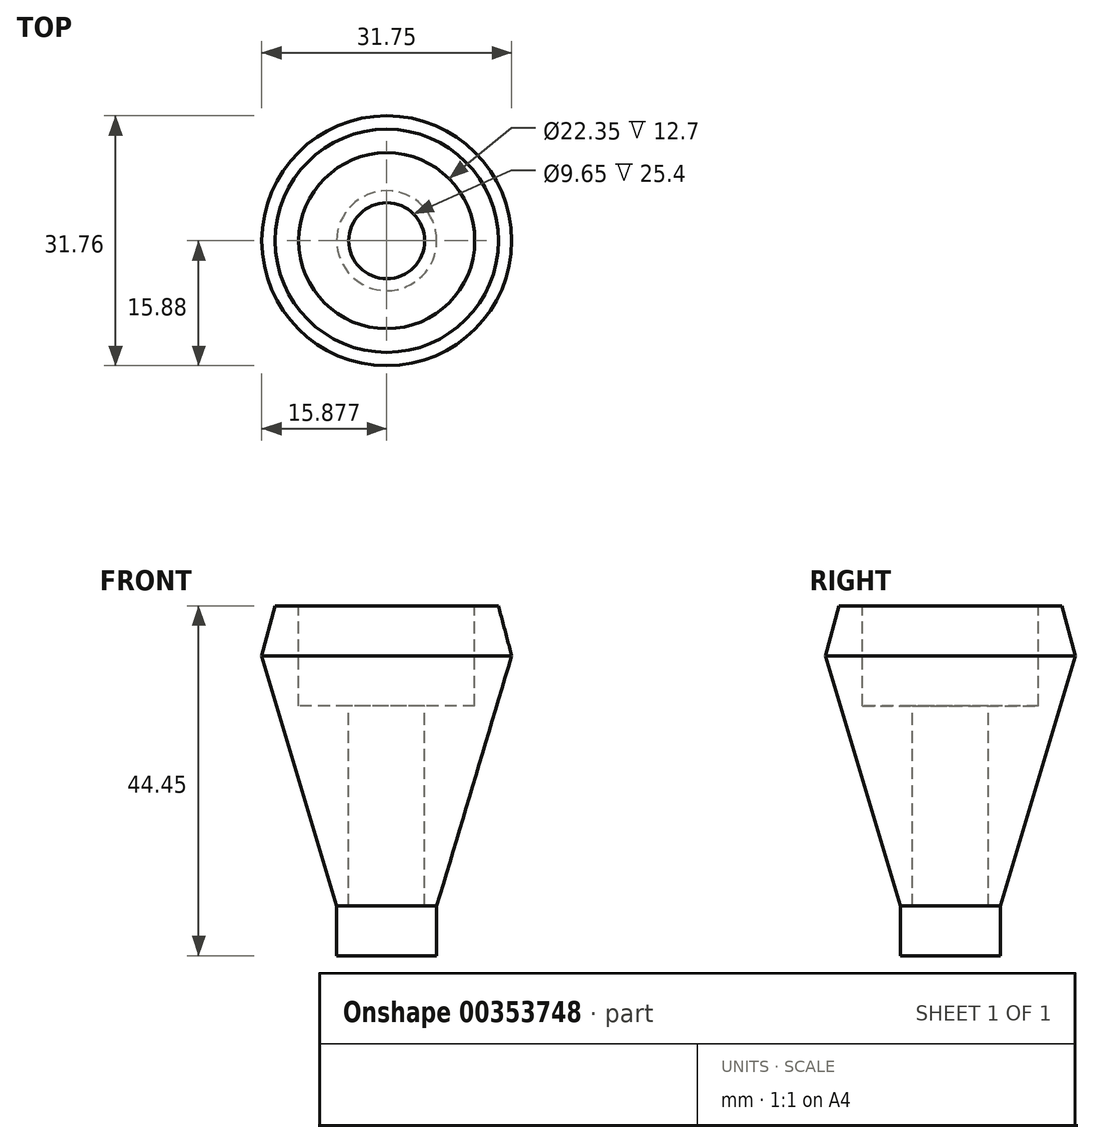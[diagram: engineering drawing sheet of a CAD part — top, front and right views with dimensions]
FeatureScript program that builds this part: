
annotation { "Feature Type Name" : "Feature", "Feature Type Description" : "" }
export const myFeature = defineFeature(function(context is Context, id is Id, definition is map)
    precondition{}
    {
        {
            var Q0;
            Q0=qCreatedBy(makeId("Front.planeOp"),FACE);
            var sketch = newSketch(context, id + "F0", { "sketchPlane" : qUnion([Q0])});
            skLineSegment(sketch, "E0", {"start": v(14.52, 0) * mm, "end": v(20.87, 0) * mm});
            skLineSegment(sketch, "E1", {"start": v(20.87, 0) * mm, "end": v(20.87, 6.35) * mm});
            skLineSegment(sketch, "E2", {"start": v(20.87, 6.35) * mm, "end": v(30.4, 38.1) * mm});
            skLineSegment(sketch, "E3", {"start": v(30.4, 38.1) * mm, "end": v(28.7, 44.45) * mm});
            skLineSegment(sketch, "E4", {"start": v(28.7, 44.45) * mm, "end": v(14.52, 44.45) * mm});
            skLineSegment(sketch, "E5", {"start": v(14.52, 44.45) * mm, "end": v(14.52, 0) * mm});
            skLineSegment(sketch, "E6", {"start": v(30.4, 38.1) * mm, "end": v(30.4, 59.53) * mm, "construction": true});
            skSolve(sketch);
        }
        {
            var Q0;
            Q0 = qSketchRegion(id + "F0", true);
            var Q1;
            Q1=sQuery(id+"F0.wireOp",EDGE,"E5");
            revolve(context, id + "F1", {"entities" : qUnion([Q0]), "axis" : qUnion([Q1]), "revolveType" : RevolveType.FULL});
        }
        {
            var Q0;
            Q0=makeQuery(id+"F1.opRevolve","SWEPT_FACE",FACE,{"disambiguationData":[OSD([sQuery(id+"F0.wireOp",EDGE,"E4")])]});
            var sketch = newSketch(context, id + "F2", { "sketchPlane" : qUnion([Q0])});
            skPoint(sketch, "E7", {"position": v(14.52, 0) * mm});
            skCircle(sketch, "E8", {"center": v(14.52, 0) * mm, "radius": 4.83 * mm});
            skCircle(sketch, "E9", {"center": v(14.52, 0) * mm, "radius": 11.18 * mm});
            skSolve(sketch);
        }
        {
            var Q0;
            Q0=makeQuery(id+"F2.imprint","IMPRINT",FACE,{"disambiguationData":[TD([[makeQuery(id+"F2.imprint","IMPRINT",EDGE,{"derivedFrom":sQuery(id+"F2.wireOp",EDGE,"E8")}),1.0]])]});
            extrude(context, id + "F3", {"entities" : qUnion([Q0]), "operationType" : NewBodyOperationType.REMOVE, "oppositeDirection" : true, "depth" : 38.1 * mm});
        }
        {
            var Q0;
            Q0=makeQuery(id+"F2.imprint","IMPRINT",FACE,{"disambiguationData":[TD([[makeQuery(id+"F2.imprint","IMPRINT",EDGE,{"derivedFrom":sQuery(id+"F2.wireOp",EDGE,"E8")}),-1.0]])]});
            extrude(context, id + "F4", {"entities" : qUnion([Q0]), "operationType" : NewBodyOperationType.REMOVE, "oppositeDirection" : true, "depth" : 12.7 * mm});
        }
    });
